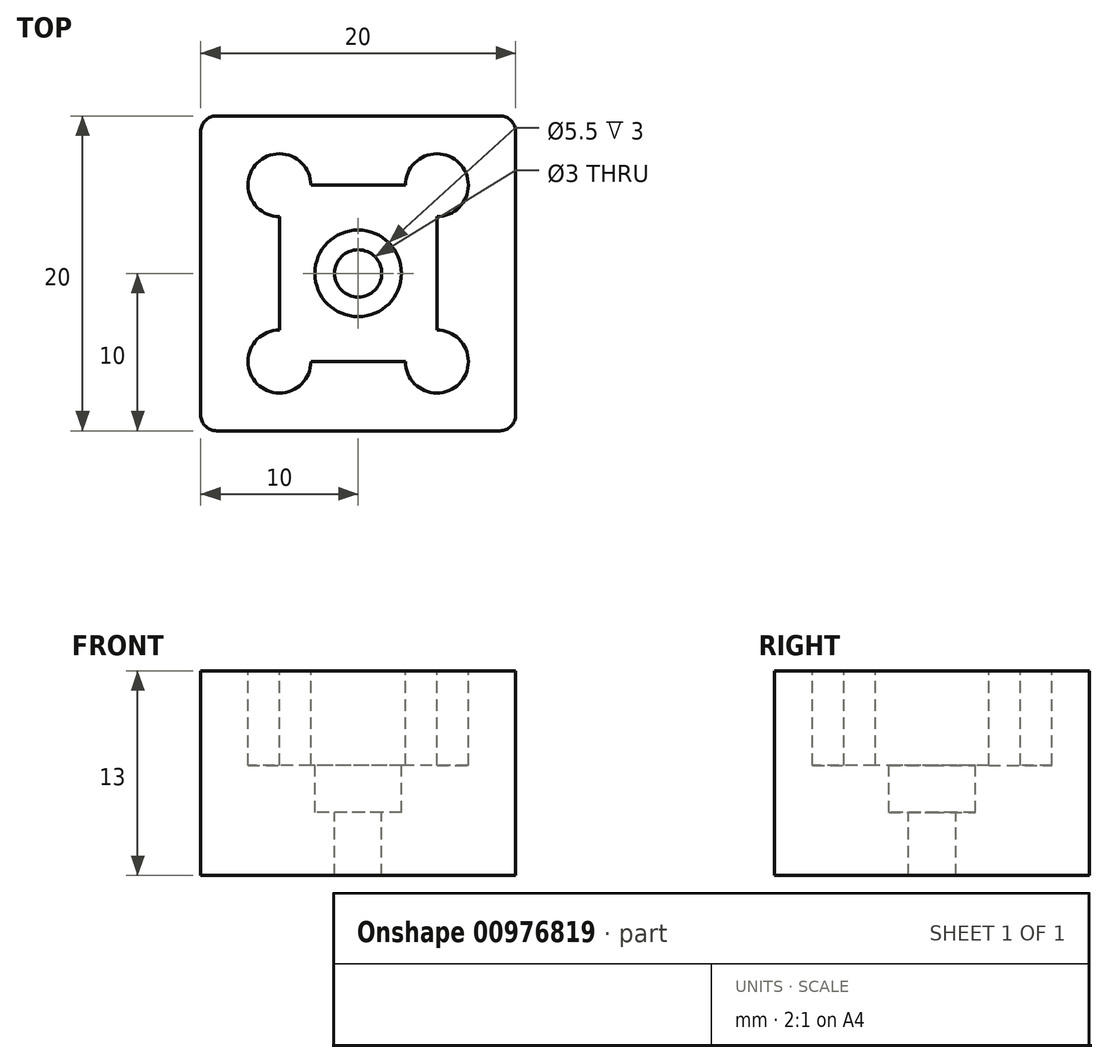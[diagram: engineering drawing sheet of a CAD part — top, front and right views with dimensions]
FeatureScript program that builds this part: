
annotation { "Feature Type Name" : "Feature", "Feature Type Description" : "" }
export const myFeature = defineFeature(function(context is Context, id is Id, definition is map)
    precondition{}
    {
        {
            var Q0;
            Q0=qCreatedBy(makeId("Top.planeOp"),FACE);
            var sketch = newSketch(context, id + "F0", { "sketchPlane" : qUnion([Q0])});
            skLineSegment(sketch, "E0.bottom", {"start": v(10, 10) * mm, "end": v(-10, 10) * mm});
            skLineSegment(sketch, "E0.top", {"start": v(10, -10) * mm, "end": v(-10, -10) * mm});
            skLineSegment(sketch, "E0.left", {"start": v(10, 10) * mm, "end": v(10, -10) * mm});
            skLineSegment(sketch, "E0.right", {"start": v(-10, 10) * mm, "end": v(-10, -10) * mm});
            skPoint(sketch, "E0.middle", {"position": v(0, 0) * mm});
            skSolve(sketch);
        }
        {
            var Q0;
            Q0=makeQuery(id+"F0.imprint","IMPRINT",FACE,{"disambiguationData":[TD([[makeQuery(id+"F0.imprint","IMPRINT",EDGE,{"derivedFrom":sQuery(id+"F0.wireOp",EDGE,"E0.bottom")}),1.0]])]});
            extrude(context, id + "F1", {"entities" : qUnion([Q0]), "depth" : 13 * mm, "offsetDistance" : 25 * mm});
        }
        {
            var Q0;
            Q0=makeQuery(id+"F1.opExtrude","SWEPT_EDGE",EDGE,{"disambiguationData":[OSD([sQuery(id+"F0.wireOp",EDGE,"E0.top"),sQuery(id+"F0.wireOp",EDGE,"E0.left")])]});
            var Q1;
            Q1=makeQuery(id+"F1.opExtrude","SWEPT_EDGE",EDGE,{"disambiguationData":[OSD([sQuery(id+"F0.wireOp",EDGE,"E0.bottom"),sQuery(id+"F0.wireOp",EDGE,"E0.left")])]});
            var Q2;
            Q2=makeQuery(id+"F1.opExtrude","SWEPT_EDGE",EDGE,{"disambiguationData":[OSD([sQuery(id+"F0.wireOp",EDGE,"E0.bottom"),sQuery(id+"F0.wireOp",EDGE,"E0.right")])]});
            var Q3;
            Q3=makeQuery(id+"F1.opExtrude","SWEPT_EDGE",EDGE,{"disambiguationData":[OSD([sQuery(id+"F0.wireOp",EDGE,"E0.top"),sQuery(id+"F0.wireOp",EDGE,"E0.right")])]});
            fillet(context, id + "F2", {"entities" : qUnion([Q0, Q1, Q2, Q3]), "radius" : 1 * mm, "tangentPropagation" : true, "allowEdgeOverflow" : false});
        }
        {
            var Q0;
            Q0=makeQuery(id+"F1.opExtrude","CAP_FACE",FACE,{"disambiguationData":[OSD([sQuery(id+"F0.wireOp",EDGE,"E0.bottom"),sQuery(id+"F0.wireOp",EDGE,"E0.top"),sQuery(id+"F0.wireOp",EDGE,"E0.left"),sQuery(id+"F0.wireOp",EDGE,"E0.right")])],"isStart":false});
            var sketch = newSketch(context, id + "F3", { "sketchPlane" : qUnion([Q0])});
            skLineSegment(sketch, "E1.bottom", {"start": v(5, 5.6) * mm, "end": v(-5, 5.6) * mm});
            skLineSegment(sketch, "E1.top", {"start": v(5, -5.6) * mm, "end": v(-5, -5.6) * mm});
            skLineSegment(sketch, "E1.left", {"start": v(5, 5.6) * mm, "end": v(5, -5.6) * mm});
            skLineSegment(sketch, "E1.right", {"start": v(-5, 5.6) * mm, "end": v(-5, -5.6) * mm});
            skPoint(sketch, "E1.middle", {"position": v(0, 0) * mm});
            skSolve(sketch);
        }
        {
            var Q0;
            Q0=makeQuery(id+"F3.imprint","IMPRINT",FACE,{"disambiguationData":[TD([[makeQuery(id+"F3.imprint","IMPRINT",EDGE,{"derivedFrom":sQuery(id+"F3.wireOp",EDGE,"E1.bottom")}),1.0]])]});
            extrude(context, id + "F4", {"entities" : qUnion([Q0]), "operationType" : NewBodyOperationType.REMOVE, "oppositeDirection" : true, "depth" : 6 * mm, "offsetDistance" : 25 * mm});
        }
        {
            var Q0;
            Q0=makeQuery(id+"F4.boolean.opBoolean","COPY",FACE,{"derivedFrom":makeQuery(id+"F4.opExtrude","CAP_FACE",FACE,{"disambiguationData":[OSD([sQuery(id+"F3.wireOp",EDGE,"E1.bottom"),sQuery(id+"F3.wireOp",EDGE,"E1.top"),sQuery(id+"F3.wireOp",EDGE,"E1.left"),sQuery(id+"F3.wireOp",EDGE,"E1.right")])],"isStart":false})});
            var sketch = newSketch(context, id + "F5", { "sketchPlane" : qUnion([Q0])});
            skCircle(sketch, "E2", {"center": v(0, 0) * mm, "radius": 2.75 * mm});
            skSolve(sketch);
        }
        {
            var Q0;
            Q0=makeQuery(id+"F5.imprint","IMPRINT",FACE,{"disambiguationData":[TD([[makeQuery(id+"F5.imprint","IMPRINT",EDGE,{"derivedFrom":sQuery(id+"F5.wireOp",EDGE,"E2")}),1.0]])]});
            extrude(context, id + "F6", {"entities" : qUnion([Q0]), "operationType" : NewBodyOperationType.REMOVE, "oppositeDirection" : true, "depth" : 3 * mm, "offsetDistance" : 25 * mm});
        }
        {
            var Q0;
            Q0=makeQuery(id+"F1.opExtrude","CAP_FACE",FACE,{"disambiguationData":[OSD([sQuery(id+"F0.wireOp",EDGE,"E0.bottom"),sQuery(id+"F0.wireOp",EDGE,"E0.top"),sQuery(id+"F0.wireOp",EDGE,"E0.left"),sQuery(id+"F0.wireOp",EDGE,"E0.right")])],"isStart":false});
            var sketch = newSketch(context, id + "F7", { "sketchPlane" : qUnion([Q0])});
            skCircle(sketch, "E3", {"center": v(-5, 5.6) * mm, "radius": 2 * mm});
            skCircle(sketch, "E4", {"center": v(5, 5.6) * mm, "radius": 2 * mm});
            skCircle(sketch, "E5", {"center": v(5, -5.6) * mm, "radius": 2 * mm});
            skCircle(sketch, "E6", {"center": v(-5, -5.6) * mm, "radius": 2 * mm});
            skSolve(sketch);
        }
        {
            var Q0;
            {var subQ0=sQuery(id+"F7.wireOp",EDGE,"E4");var subQ1=makeQuery(id+"F4.boolean.opBoolean","COPY",EDGE,{"derivedFrom":makeQuery(id+"F4.opExtrude","CAP_EDGE",EDGE,{"disambiguationData":[OSD([sQuery(id+"F3.wireOp",EDGE,"E1.bottom")])],"isStart":true})});var subQ2=makeQuery(id+"F7.imprint","INTERSECT",VERTEX,{"derivedFrom":[subQ1,subQ0]});Q0=makeQuery(id+"F7.imprint","IMPRINT",FACE,{"disambiguationData":[TD([[makeQuery(id+"F7.imprint","IMPRINT",EDGE,{"disambiguationData":[TD([[subQ2,1.0]])],"derivedFrom":subQ0}),1.0]])]});}
            var Q1;
            {var subQ0=sQuery(id+"F7.wireOp",EDGE,"E6");var subQ1=makeQuery(id+"F4.boolean.opBoolean","COPY",EDGE,{"derivedFrom":makeQuery(id+"F4.opExtrude","CAP_EDGE",EDGE,{"disambiguationData":[OSD([sQuery(id+"F3.wireOp",EDGE,"E1.top")])],"isStart":true})});var subQ2=makeQuery(id+"F7.imprint","INTERSECT",VERTEX,{"derivedFrom":[subQ1,subQ0]});Q1=makeQuery(id+"F7.imprint","IMPRINT",FACE,{"disambiguationData":[TD([[makeQuery(id+"F7.imprint","IMPRINT",EDGE,{"disambiguationData":[TD([[subQ2,1.0]])],"derivedFrom":subQ0}),1.0]])]});}
            var Q2;
            {var subQ0=sQuery(id+"F7.wireOp",EDGE,"E5");var subQ1=makeQuery(id+"F4.boolean.opBoolean","COPY",EDGE,{"derivedFrom":makeQuery(id+"F4.opExtrude","CAP_EDGE",EDGE,{"disambiguationData":[OSD([sQuery(id+"F3.wireOp",EDGE,"E1.top")])],"isStart":true})});var subQ2=makeQuery(id+"F7.imprint","INTERSECT",VERTEX,{"derivedFrom":[subQ1,subQ0]});Q2=makeQuery(id+"F7.imprint","IMPRINT",FACE,{"disambiguationData":[TD([[makeQuery(id+"F7.imprint","IMPRINT",EDGE,{"disambiguationData":[TD([[subQ2,-1.0]])],"derivedFrom":subQ0}),1.0]])]});}
            var Q3;
            {var subQ0=sQuery(id+"F7.wireOp",EDGE,"E3");var subQ1=makeQuery(id+"F4.boolean.opBoolean","COPY",EDGE,{"derivedFrom":makeQuery(id+"F4.opExtrude","CAP_EDGE",EDGE,{"disambiguationData":[OSD([sQuery(id+"F3.wireOp",EDGE,"E1.bottom")])],"isStart":true})});var subQ2=makeQuery(id+"F7.imprint","INTERSECT",VERTEX,{"derivedFrom":[subQ1,subQ0]});Q3=makeQuery(id+"F7.imprint","IMPRINT",FACE,{"disambiguationData":[TD([[makeQuery(id+"F7.imprint","IMPRINT",EDGE,{"disambiguationData":[TD([[subQ2,-1.0]])],"derivedFrom":subQ0}),1.0]])]});}
            extrude(context, id + "F8", {"entities" : qUnion([Q0, Q1, Q2, Q3]), "operationType" : NewBodyOperationType.REMOVE, "oppositeDirection" : true, "depth" : 6 * mm, "offsetDistance" : 25 * mm});
        }
        {
            var Q0;
            Q0=makeQuery(id+"F6.boolean.opBoolean","COPY",FACE,{"derivedFrom":makeQuery(id+"F6.opExtrude","CAP_FACE",FACE,{"disambiguationData":[OSD([sQuery(id+"F5.wireOp",EDGE,"E2")])],"isStart":false})});
            var sketch = newSketch(context, id + "F9", { "sketchPlane" : qUnion([Q0])});
            skCircle(sketch, "E7", {"center": v(0, 0) * mm, "radius": 1.5 * mm});
            skSolve(sketch);
        }
        {
            var Q0;
            Q0=makeQuery(id+"F9.imprint","IMPRINT",FACE,{"disambiguationData":[TD([[makeQuery(id+"F9.imprint","IMPRINT",EDGE,{"derivedFrom":sQuery(id+"F9.wireOp",EDGE,"E7")}),1.0]])]});
            extrude(context, id + "F10", {"entities" : qUnion([Q0]), "operationType" : NewBodyOperationType.REMOVE, "endBound" : BoundingType.THROUGH_ALL, "oppositeDirection" : true, "depth" : 25 * mm, "offsetDistance" : 25 * mm});
        }
    });
